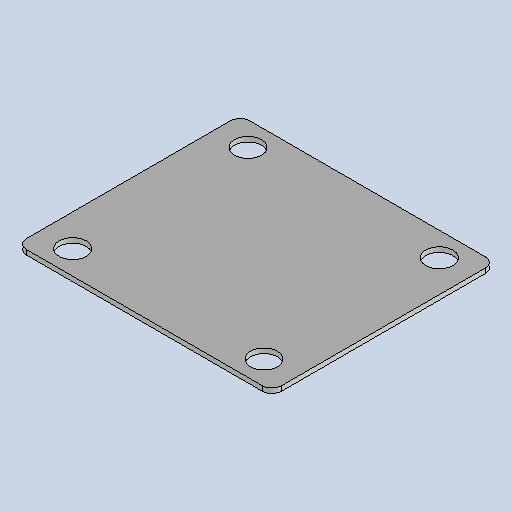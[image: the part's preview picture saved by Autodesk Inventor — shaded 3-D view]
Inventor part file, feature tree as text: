
AUTODESK INVENTOR PART (.ipt)
format: ipt  version: 2025 (Build 290162010, 162A)  size: 167,936 bytes
history: native  units: mm
features: sketch x2, sheet_metal_op x1, chamfer x1, other x1
ambient origin geometry x8: Origin, YZ Plane, XZ Plane, XY Plane, X Axis, Y Axis, Z Axis, Center Point
bodies: Solid1 (feature_tree)
feature tree (5):
  sketch  "3D Sketch1"
  sheet_metal_op  "Face1"
  chamfer  "Corner Round1"
  sketch  "Sketch1"  dims[d0=50.0mm d1=23.865632mm d2=8.726646mm d6=3.0mm d30=140.0mm d34=160.0mm d35=17.0mm d36=20.0mm d37=15.0mm d38=6.0mm]
  other  "Plate1"
